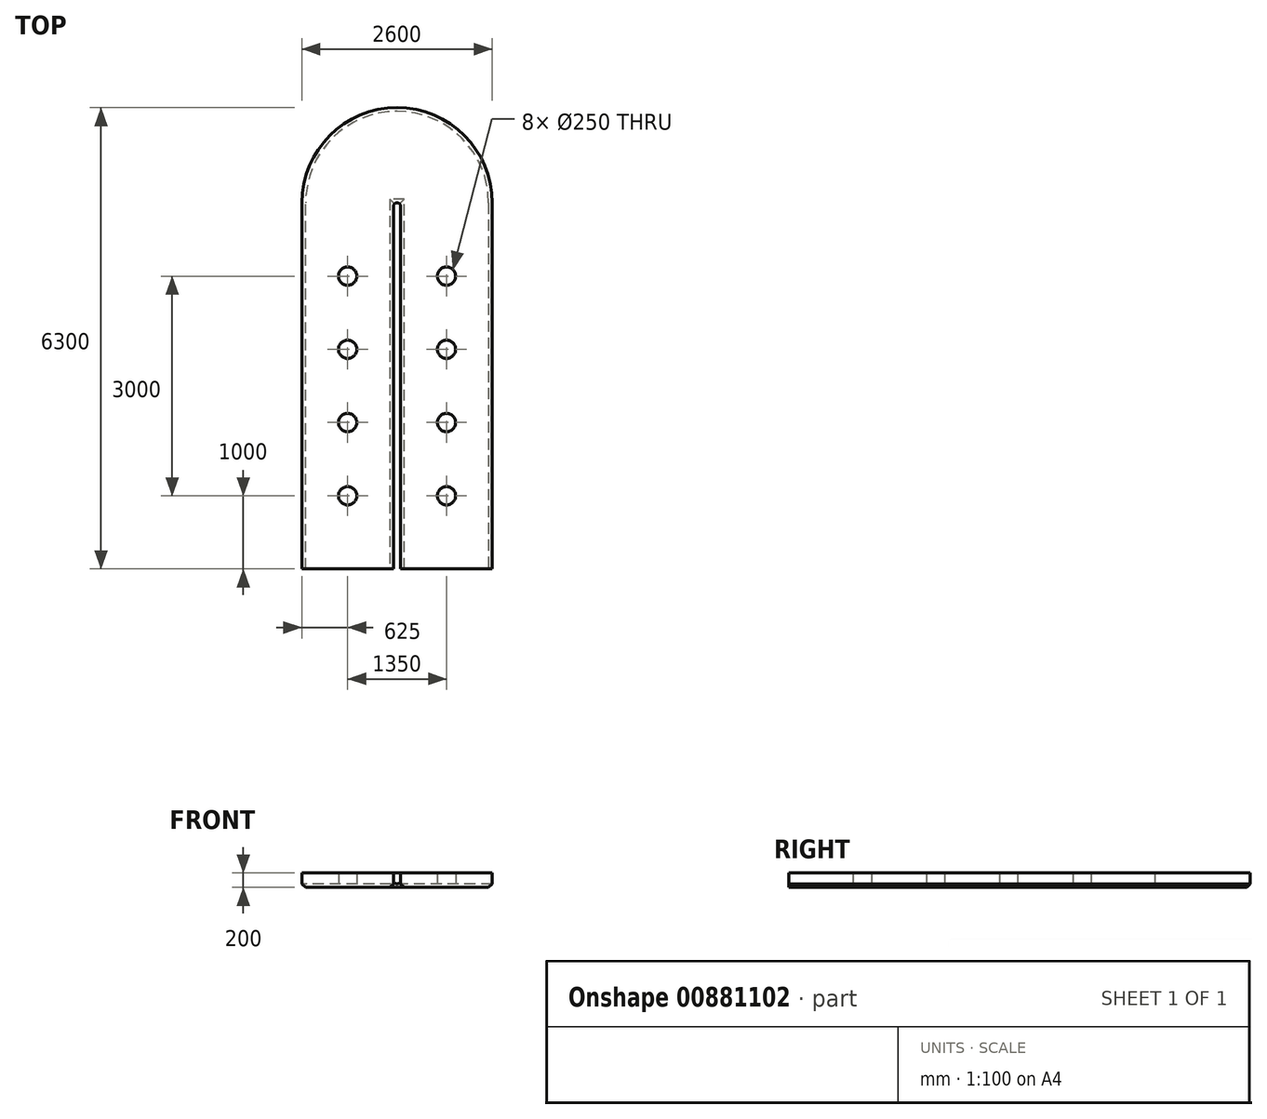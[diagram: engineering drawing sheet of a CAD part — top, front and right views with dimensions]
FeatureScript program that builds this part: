
annotation { "Feature Type Name" : "Feature", "Feature Type Description" : "" }
export const myFeature = defineFeature(function(context is Context, id is Id, definition is map)
    precondition{}
    {
        {
            var Q0;
            Q0=qCreatedBy(makeId("Top.planeOp"),FACE);
            var sketch = newSketch(context, id + "F0", { "sketchPlane" : qUnion([Q0])});
            skLineSegment(sketch, "E0", {"start": v(0, 0) * mm, "end": v(50, 0) * mm});
            skLineSegment(sketch, "E1", {"start": v(50, 0) * mm, "end": v(50, -5000) * mm});
            skLineSegment(sketch, "E2", {"start": v(0, 0) * mm, "end": v(-50, 0) * mm});
            skLineSegment(sketch, "E3", {"start": v(-50, 0) * mm, "end": v(-50, -5000) * mm});
            skLineSegment(sketch, "E4", {"start": v(50, -5000) * mm, "end": v(1300, -5000) * mm});
            skLineSegment(sketch, "E5", {"start": v(1300, -5000) * mm, "end": v(1300, 0) * mm});
            skLineSegment(sketch, "E6", {"start": v(-50, -5000) * mm, "end": v(-1300, -5000) * mm});
            skLineSegment(sketch, "E7", {"start": v(-1300, -5000) * mm, "end": v(-1300, 0) * mm});
            skArc(sketch, "E8", {"start": v(-1300, 0) * mm, "mid": v(0, 1300) * mm, "end": v(1300, 0) * mm});
            skLineSegment(sketch, "E9", {"start": v(0, 0) * mm, "end": v(0, -5000) * mm, "construction": true});
            skCircle(sketch, "E10", {"center": v(675, -1000) * mm, "radius": 125 * mm});
            skCircle(sketch, "E11.MirrorC", {"center": v(-675, -1000) * mm, "radius": 125 * mm});
            skCircle(sketch, "E12", {"center": v(675, -2000) * mm, "radius": 125 * mm});
            skCircle(sketch, "E13", {"center": v(675, -3000) * mm, "radius": 125 * mm});
            skCircle(sketch, "E14", {"center": v(675, -4000) * mm, "radius": 125 * mm});
            skCircle(sketch, "E15.MirrorC", {"center": v(-675, -2000) * mm, "radius": 125 * mm});
            skCircle(sketch, "E16.MirrorC", {"center": v(-675, -3000) * mm, "radius": 125 * mm});
            skCircle(sketch, "E17.MirrorC", {"center": v(-675, -4000) * mm, "radius": 125 * mm});
            skSolve(sketch);
        }
        {
            var Q0;
            Q0=makeQuery(id+"F0.imprint","IMPRINT",FACE,{"disambiguationData":[TD([[makeQuery(id+"F0.imprint","IMPRINT",EDGE,{"derivedFrom":sQuery(id+"F0.wireOp",EDGE,"E0")}),1.0]])]});
            extrude(context, id + "F1", {"entities" : qUnion([Q0]), "depth" : 200 * mm, "offsetDistance" : 25 * mm});
        }
        {
            var Q0;
            Q0=makeQuery(id+"F1.opExtrude","CAP_EDGE",EDGE,{"disambiguationData":[OSD([sQuery(id+"F0.wireOp",EDGE,"E5")])],"isStart":true});
            var Q1;
            Q1=makeQuery(id+"F1.opExtrude","CAP_EDGE",EDGE,{"disambiguationData":[OSD([sQuery(id+"F0.wireOp",EDGE,"E8")])],"isStart":true});
            var Q2;
            Q2=makeQuery(id+"F1.opExtrude","CAP_EDGE",EDGE,{"disambiguationData":[OSD([sQuery(id+"F0.wireOp",EDGE,"E7")])],"isStart":true});
            var Q3;
            Q3=makeQuery(id+"F1.opExtrude","CAP_EDGE",EDGE,{"disambiguationData":[OSD([sQuery(id+"F0.wireOp",EDGE,"E1")])],"isStart":true});
            var Q4;
            Q4=makeQuery(id+"F1.opExtrude","CAP_EDGE",EDGE,{"disambiguationData":[OSD([sQuery(id+"F0.wireOp",EDGE,"E3")])],"isStart":true});
            var Q5;
            Q5=makeQuery(id+"F1.opExtrude","CAP_EDGE",EDGE,{"disambiguationData":[OSD([sQuery(id+"F0.wireOp",EDGE,"E0"),sQuery(id+"F0.wireOp",EDGE,"E2")])],"isStart":true});
            chamfer(context, id + "F2", {"entities" : qUnion([Q0, Q1, Q2, Q3, Q4, Q5]), "width" : 50 * mm, "tangentPropagation" : true});
        }
        {
            var Q0;
            Q0=makeQuery(id+"F1.opExtrude","SWEPT_EDGE",EDGE,{"disambiguationData":[OSD([sQuery(id+"F0.wireOp",EDGE,"E2"),sQuery(id+"F0.wireOp",EDGE,"E3")])]});
            var Q1;
            Q1=makeQuery(id+"F1.opExtrude","SWEPT_EDGE",EDGE,{"disambiguationData":[OSD([sQuery(id+"F0.wireOp",EDGE,"E0"),sQuery(id+"F0.wireOp",EDGE,"E1")])]});
            fillet(context, id + "F3", {"entities" : qUnion([Q0, Q1]), "radius" : 50 * mm, "tangentPropagation" : true, "allowEdgeOverflow" : false});
        }
    });
